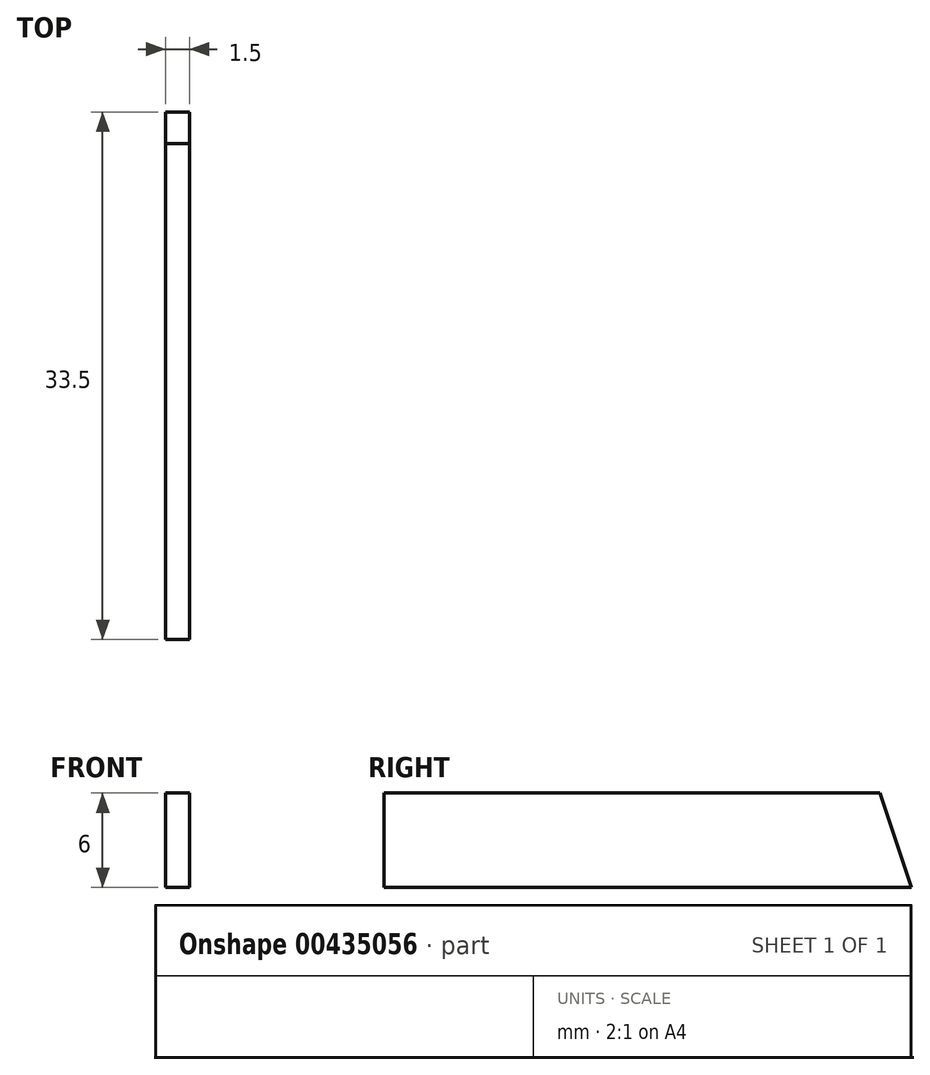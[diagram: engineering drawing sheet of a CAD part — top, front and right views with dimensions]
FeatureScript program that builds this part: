
annotation { "Feature Type Name" : "Feature", "Feature Type Description" : "" }
export const myFeature = defineFeature(function(context is Context, id is Id, definition is map)
    precondition{}
    {
        {
            var Q0;
            Q0=qCreatedBy(makeId("Right.planeOp"),FACE);
            var sketch = newSketch(context, id + "F0", { "sketchPlane" : qUnion([Q0])});
            skLineSegment(sketch, "E0", {"start": v(0, 0) * mm, "end": v(0, 6) * mm});
            skLineSegment(sketch, "E1", {"start": v(0, 6) * mm, "end": v(31.5, 6) * mm});
            skLineSegment(sketch, "E2", {"start": v(31.5, 6) * mm, "end": v(33.5, 0) * mm});
            skLineSegment(sketch, "E3", {"start": v(33.5, 0) * mm, "end": v(0, 0) * mm});
            skSolve(sketch);
        }
        {
            var Q0;
            Q0 = qSketchRegion(id + "F0", true);
            extrude(context, id + "F1", {"entities" : qUnion([Q0]), "depth" : 1.5 * mm});
        }
    });
